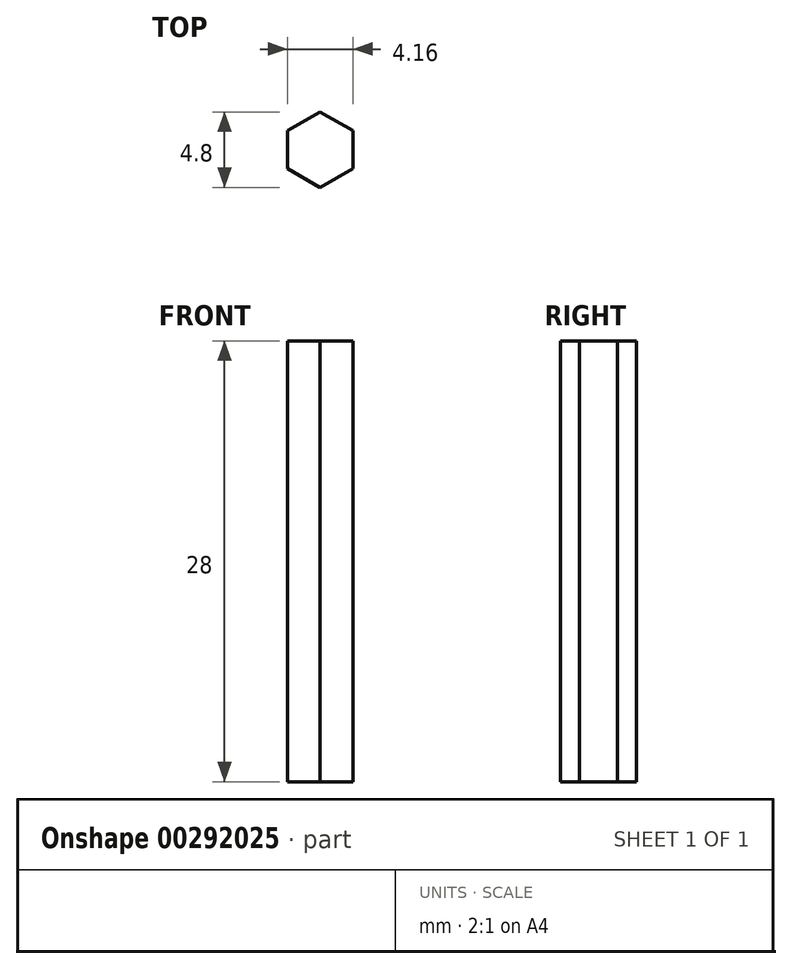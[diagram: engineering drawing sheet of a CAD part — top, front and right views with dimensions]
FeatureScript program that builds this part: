
annotation { "Feature Type Name" : "Feature", "Feature Type Description" : "" }
export const myFeature = defineFeature(function(context is Context, id is Id, definition is map)
    precondition{}
    {
        {
            var Q0;
            Q0=qCreatedBy(makeId("Top.planeOp"),FACE);
            var sketch = newSketch(context, id + "F0", { "sketchPlane" : qUnion([Q0])});
            skCircle(sketch, "E0.cCircle", {"center": v(0, 0) * mm, "radius": 2.08 * mm, "construction": true});
            skLineSegment(sketch, "E0.0", {"start": v(-2.08, 1.2) * mm, "end": v(0, 2.4) * mm});
            skLineSegment(sketch, "E0.1", {"start": v(0, 2.4) * mm, "end": v(2.08, 1.2) * mm});
            skLineSegment(sketch, "E0.2", {"start": v(2.08, 1.2) * mm, "end": v(2.08, -1.2) * mm});
            skLineSegment(sketch, "E0.3", {"start": v(2.08, -1.2) * mm, "end": v(0, -2.4) * mm});
            skLineSegment(sketch, "E0.4", {"start": v(0, -2.4) * mm, "end": v(-2.08, -1.2) * mm});
            skLineSegment(sketch, "E0.5", {"start": v(-2.08, -1.2) * mm, "end": v(-2.08, 1.2) * mm});
            skPoint(sketch, "E0.0.midPoint", {"position": v(-1.04, 1.8) * mm});
            skSolve(sketch);
        }
        {
            var Q0;
            Q0 = qSketchRegion(id + "F0", true);
            extrude(context, id + "F1", {"entities" : qUnion([Q0]), "depth" : 28 * mm});
        }
    });
